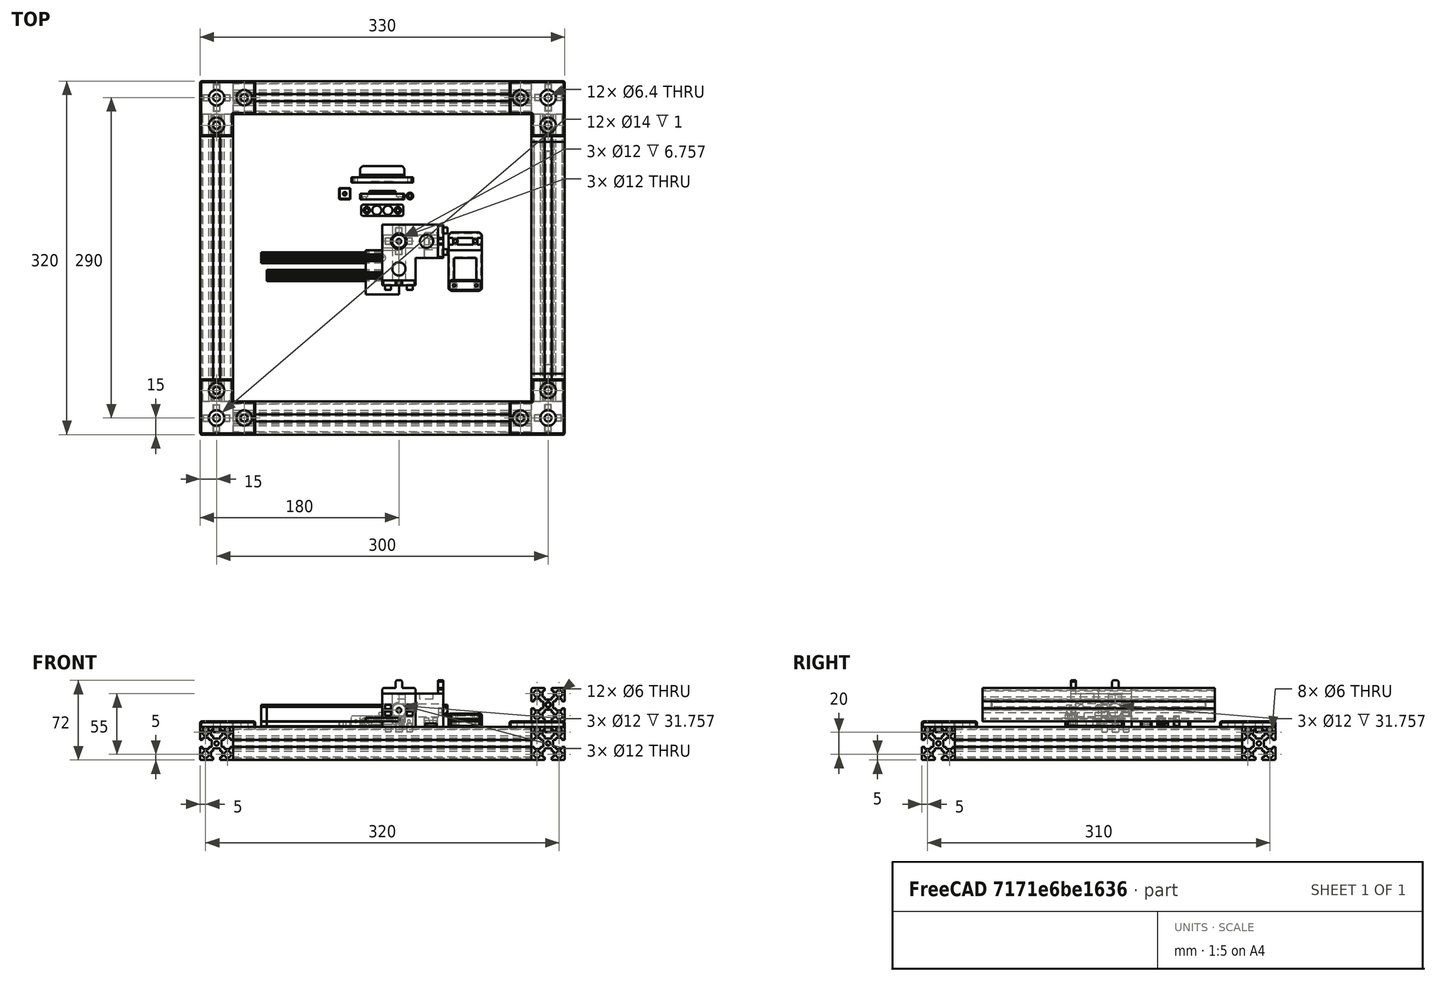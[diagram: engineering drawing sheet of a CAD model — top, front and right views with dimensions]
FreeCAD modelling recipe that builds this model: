
FCSTD DOCUMENT  (FreeCAD 0.18R16146 (Git))
Label: hophat-3030
License: All rights reserved
LicenseURL: http://en.wikipedia.org/wiki/All_rights_reserved
objects: Part::Box×32, Part::Feature×28, Part::MultiFuse×27, Part::Chamfer×27, Part::Cylinder×21, Part::Cut×17, Part::Fillet×2, Part::MultiCommon×1
note: 155 computed .brp shape members not serialized (recipe doc carries the construction recipe); baked Part::Feature solids carry a one-line shape summary decoded from their .brp

FEATURE [Part::Feature] Fusion025  label="extrusion-260-003"
  Placement = pos=(-150,-130,350) rot=(-1,0,0;1.5708rad)
  shape: bbox 30 x 260 x 30 mm, 63 faces (baked)
FEATURE [Part::Feature] Fusion032  label="extrusion-270-005"
  Placement = pos=(-135,-145,350) rot=(0,1,0;1.5708rad)
  shape: bbox 270 x 30 x 30 mm, 63 faces (baked)
FEATURE [Part::Feature] Fusion026  label="extrusion-260-004"
  Placement = pos=(150,-130,350) rot=(-1,0,0;1.5708rad)
  shape: bbox 30 x 260 x 30 mm, 63 faces (baked)
FEATURE [Part::Feature] Fusion031  label="extrusion-270-004"
  Placement = pos=(-135,145,350) rot=(0,1,0;1.5708rad)
  shape: bbox 270 x 30 x 30 mm, 63 faces (baked)
FEATURE [Part::MultiFuse] Fusion004003058  label="__top-framr-pref"
  Placement = pos=(0,0,-365) rot=(0,0,1;0rad)
  Shapes = -> [Fusion025,Fusion031,Fusion026,Fusion032]
FEATURE [Part::Feature] Fusion020006007003002004  label="top-joiner-002"
  Placement = pos=(-150,-145,370) rot=(0.707107,0.707107,0;3.14159rad)
  shape: bbox 50 x 50 x 10 mm, 87 faces (baked)
FEATURE [Part::Feature] Fusion020006007003002005  label="top-joiner-003"
  Placement = pos=(-150,145,370) rot=(1,0,0;3.14159rad)
  shape: bbox 50 x 50 x 10 mm, 87 faces (baked)
FEATURE [Part::Feature] Fusion020006007003002006  label="top-joiner-004"
  Placement = pos=(150,145,370) rot=(0.707107,-0.707107,0;3.14159rad)
  shape: bbox 50 x 50 x 10 mm, 87 faces (baked)
FEATURE [Part::Feature] Fusion020006007003002007  label="top-joiner-001"
  Placement = pos=(150,-145,370) rot=(0,1,0;3.14159rad)
  shape: bbox 50 x 50 x 10 mm, 87 faces (baked)
FEATURE [Part::Cylinder] Cylinder
  Angle = 360
  AttacherType = Attacher::AttachEngine3D
  Height = 10
  Radius = 1.25
FEATURE [Part::Cylinder] Cylinder001
  Angle = 360
  AttacherType = Attacher::AttachEngine3D
  Height = 3
  Placement = pos=(0,0,10) rot=(0,0,1;0rad)
  Radius = 3
FEATURE [Part::MultiFuse] Fusion020006007003002009  label="_M3-self-tapping"
  Shapes = -> [Cylinder001,Cylinder]
FEATURE [Part::Cylinder] Cylinder002
  Angle = 360
  AttacherType = Attacher::AttachEngine3D
  Height = 10
  Radius = 1.65
FEATURE [Part::Cylinder] Cylinder003
  Angle = 360
  AttacherType = Attacher::AttachEngine3D
  Height = 3
  Placement = pos=(0,0,10) rot=(0,0,1;0rad)
  Radius = 3
FEATURE [Part::MultiFuse] Fusion020006007003002010  label="_M3-outer-slot"
  Shapes = -> [Cylinder002,Cylinder003]
FEATURE [Part::Box] Box  label="Cube"
  AttacherType = Attacher::AttachEngine3D
  Height = 30
  Length = 30
  Width = 30
FEATURE [Part::Feature] Fusion020006007003002011  label="top-joiner-005"
  Placement = pos=(15,15,-5) rot=(0,0,1;0rad)
  shape: bbox 50 x 50 x 10 mm, 87 faces (baked)
FEATURE [Part::Box] Box001  label="Cube001"
  AttacherType = Attacher::AttachEngine3D
  Height = 30
  Length = 30
  Placement = pos=(0,-25,0) rot=(0,0,1;0rad)
  Width = 25
FEATURE [Part::Box] Box002  label="Cube002"
  AttacherType = Attacher::AttachEngine3D
  Height = 30
  Length = 25
  Placement = pos=(30,0,0) rot=(0,0,1;0rad)
  Width = 30
FEATURE [Part::Cylinder] Cylinder004
  Angle = 360
  AttacherType = Attacher::AttachEngine3D
  Height = 26
  Placement = pos=(15,15,4) rot=(0,0,1;0rad)
  Radius = 6
FEATURE [Part::Cylinder] Cylinder005
  Angle = 360
  AttacherType = Attacher::AttachEngine3D
  Height = 10
  Placement = pos=(45,15,15) rot=(0,1,0;1.5708rad)
  Radius = 2.2
FEATURE [Part::Cylinder] Cylinder006
  Angle = 360
  AttacherType = Attacher::AttachEngine3D
  Height = 10
  Placement = pos=(15,-15,15) rot=(1,0,0;1.5708rad)
  Radius = 2.2
FEATURE [Part::Cylinder] Cylinder007
  Angle = 360
  AttacherType = Attacher::AttachEngine3D
  Height = 51
  Placement = pos=(0,15,15) rot=(0,1,0;1.5708rad)
  Radius = 6
FEATURE [Part::Cylinder] Cylinder009
  Angle = 360
  AttacherType = Attacher::AttachEngine3D
  Height = 30
  Placement = pos=(15,15,0) rot=(0,0,1;0rad)
  Radius = 2.2
FEATURE [Part::Cylinder] Cylinder008
  Angle = 360
  AttacherType = Attacher::AttachEngine3D
  Height = 51
  Placement = pos=(15,30,15) rot=(1,0,0;1.5708rad)
  Radius = 6
FEATURE [Part::Cylinder] Cylinder010
  Angle = 360
  AttacherType = Attacher::AttachEngine3D
  Height = 5
  Placement = pos=(40,15,25) rot=(0,0,1;0rad)
  Radius = 6
FEATURE [Part::Cylinder] Cylinder011
  Angle = 360
  AttacherType = Attacher::AttachEngine3D
  Height = 5
  Placement = pos=(15,-10,25) rot=(0,0,1;0rad)
  Radius = 6
FEATURE [Part::MultiFuse] Fusion020006007003002012  label="bottom-cut-slot"
  Shapes = -> [Cylinder011,Cylinder010]
FEATURE [Part::Box] Box003  label="Cube003"
  AttacherType = Attacher::AttachEngine3D
  Height = 10
  Length = 5.3
  Placement = pos=(2.6,-24,10) rot=(0,0,1;0rad)
  Width = 5
FEATURE [Part::Box] Box004  label="Cube004"
  AttacherType = Attacher::AttachEngine3D
  Height = 10
  Length = 5.3
  Placement = pos=(22.1,-24,10) rot=(0,0,1;0rad)
  Width = 5
FEATURE [Part::MultiFuse] Fusion
  Shapes = -> [Box001,Box002,Box]
FEATURE [Part::MultiFuse] Fusion020006007003002013004  label="corner-inner-cut"
  Shapes = -> [Cylinder009,Cylinder006,Cylinder007,Cylinder005,Cylinder004,Cylinder008]
FEATURE [Part::Cut] Cut  label="corner-base"
  Base = -> Fusion
  Tool = -> Fusion020006007003002013004
FEATURE [Part::Box] Box005  label="Cube005"
  AttacherType = Attacher::AttachEngine3D
  Height = 6
  Length = 30
  Placement = pos=(0,-25,29) rot=(0,0,1;0rad)
  Width = 4.5
FEATURE [Part::Box] Box006  label="Cube006"
  AttacherType = Attacher::AttachEngine3D
  Height = 7
  Length = 6
  Placement = pos=(12,-25,35) rot=(0,0,1;0rad)
  Width = 4.5
FEATURE [Part::Box] Box007  label="Cube007"
  AttacherType = Attacher::AttachEngine3D
  Height = 10
  Length = 30
  Width = 30
FEATURE [Part::MultiCommon] Common
  Placement = pos=(30,0,7e-15) rot=(0,1,0;3.14159rad)
  Shapes = -> [Box007,Fusion020006007003002011]
FEATURE [Part::Chamfer] Chamfer005002
  Base = -> Box005
  Edges = 2 edges r=1: [Edge2,Edge6]
FEATURE [Part::MultiFuse] Fusion020006007003002013006002005002
  Shapes = -> [Box006,Chamfer005002]
FEATURE [Part::Feature] Fusion020006007003002013006002005002001  label="Fusion020006007003002013006002005003"
  Placement = pos=(30,-7e-15,0) rot=(0,0,1;1.5708rad)
  shape: bbox 4.5 x 30 x 13 mm, 14 faces (baked)
FEATURE [Part::Chamfer] Chamfer005003
  Base = -> Fusion020006007003002013006002005002001
  Edges = 2 edges r=1: [Edge31,Edge32]
FEATURE [Part::Chamfer] Chamfer005004
  Base = -> Fusion020006007003002013006002005002
  Edges = 2 edges r=1: [Edge31,Edge32]
FEATURE [Part::Feature] Fusion020006007003002013006002005002002010  label="210mm-extrusion-004"
  Placement = pos=(150,105,20) rot=(1,0,0;1.5708rad)
  shape: bbox 30 x 210 x 30 mm, 69 faces (baked)
FEATURE [Part::MultiFuse] Fusion020006007003002013006002005002002014
  Shapes = -> [Chamfer005004,Chamfer005003]
FEATURE [Part::MultiFuse] Fusion020006007003002013006002005002002015
  Placement = pos=(0,-5,0) rot=(0,0,1;0rad)
  Shapes = -> [Box004,Box003]
FEATURE [Part::Feature] Fusion020006007003002013006002005002002015001  label="Fusion020006007003002013006002005002002016"
  Placement = pos=(35,-7.8e-15,0) rot=(0,0,1;1.5708rad)
  shape: bbox 5 x 24.8 x 10 mm, 12 faces, 2 solids (baked)
FEATURE [Part::MultiFuse] Fusion020006007003002013006002005002002015002  label="side-aligner"
  Shapes = -> [Fusion020006007003002013006002005002002015001,Fusion020006007003002013006002005002002015]
FEATURE [Part::MultiFuse] Fusion020006007003002008  label="__top-joiner-pref"
  Placement = pos=(0,0,-365) rot=(0,0,1;0rad)
  Shapes = -> [Fusion020006007003002007,Fusion020006007003002004,Fusion020006007003002006,Fusion020006007003002005]
FEATURE [Part::Feature] Fusion020006007003002013006002005002002015002001  label="side-aligner001"
  shape: bbox 56.4 x 56.4 x 10 mm, 24 faces, 4 solids (baked)
FEATURE [Part::Feature] Cut001  label="corner-base001"
  shape: bbox 55 x 55 x 30 mm, 20 faces (baked)
FEATURE [Part::Chamfer] Chamfer
  Base = -> Fusion020006007003002013006002005002002015002001
  Edges = 4 edges r=4: [Edge10,Edge22,Edge34,Edge46]
FEATURE [Part::Fillet] Fillet
  Base = -> Cut001
  Edges = 10 edges r=1: [Edge31,Edge32,Edge33,Edge36,Edge38,Edge54,Edge55,Edge56,Edge57,Edge58]
FEATURE [Part::Chamfer] Chamfer005005
  Base = -> Fillet
  Edges = 3 edges r=1: [Edge23,Edge34,Edge76]
FEATURE [Part::MultiFuse] Fusion020006007003002013006002005002002015002002  label="top-r1"
  Shapes = -> [Chamfer005005,Chamfer,Common]
FEATURE [Part::Feature] Cut002  label="corner-base002"
  shape: bbox 55 x 55 x 30 mm, 20 faces (baked)
FEATURE [Part::Feature] Fusion020006007003002013006002005002002015002003  label="side-aligner002"
  shape: bbox 56.4 x 56.4 x 10 mm, 24 faces, 4 solids (baked)
FEATURE [Part::Chamfer] Chamfer005006
  Base = -> Fusion020006007003002013006002005002002015002003
  Edges = 4 edges r=4: [Edge9,Edge21,Edge33,Edge45]
FEATURE [Part::Fillet] Fillet001
  Base = -> Cut002
  Edges = 10 edges r=1: [Edge31,Edge32,Edge33,Edge36,Edge38,Edge54,Edge55,Edge56,Edge57,Edge58]
FEATURE [Part::MultiFuse] Fusion020006007003002013006002005002002015002004
  Shapes = -> [Fillet001,Chamfer005006,Fusion020006007003002013006002005002002014]
FEATURE [Part::Chamfer] Chamfer005007
  Base = -> Fusion020006007003002013006002005002002015002004
  Edges = 3 edges r=1: [Edge35,Edge113,Edge145]
FEATURE [Part::Cut] Cut003  label="bottom-r1"
  Base = -> Chamfer005007
  Tool = -> Fusion020006007003002012
FEATURE [Part::Box] Box008  label="Cube008"
  AttacherType = Attacher::AttachEngine3D
  Height = 5.2
  Length = 38
  Placement = pos=(-19,-5,0) rot=(0,0,1;0rad)
  Width = 10
FEATURE [Part::Cylinder] Cylinder012
  Angle = 360
  AttacherType = Attacher::AttachEngine3D
  Height = 3
  Placement = pos=(-5,0,2.2) rot=(0,0,1;0rad)
  Radius = 4.15
FEATURE [Part::Cylinder] Cylinder013
  Angle = 360
  AttacherType = Attacher::AttachEngine3D
  Height = 3
  Placement = pos=(5,0,2.2) rot=(0,0,1;0rad)
  Radius = 4.15
FEATURE [Part::Cylinder] Cylinder014
  Angle = 360
  AttacherType = Attacher::AttachEngine3D
  Height = 10
  Placement = pos=(-14,0,0) rot=(0,0,1;0rad)
  Radius = 1.7
FEATURE [Part::Cylinder] Cylinder015
  Angle = 360
  AttacherType = Attacher::AttachEngine3D
  Height = 10
  Placement = pos=(14,0,0) rot=(0,0,1;0rad)
  Radius = 1.7
FEATURE [Part::Cylinder] Cylinder016
  Angle = 360
  AttacherType = Attacher::AttachEngine3D
  Height = 2
  Placement = pos=(14,0,0) rot=(0,0,1;0rad)
  Radius = 3
FEATURE [Part::Cylinder] Cylinder017
  Angle = 360
  AttacherType = Attacher::AttachEngine3D
  Height = 2
  Placement = pos=(-14,0,0) rot=(0,0,1;0rad)
  Radius = 3
FEATURE [Part::MultiFuse] Fusion020006007003002013006002005002002015002005
  Placement = pos=(0,0,4) rot=(0,0,1;0rad)
  Shapes = -> [Cylinder017,Cylinder016]
FEATURE [Part::MultiFuse] Fusion020006007003002013006002005002002015002006
  Shapes = -> [Cylinder014,Cylinder015]
FEATURE [Part::Chamfer] Chamfer005008
  Base = -> Box008
  Edges = 4 edges r=1: [Edge1,Edge3,Edge5,Edge7]
FEATURE [Part::Cut] Cut004
  Base = -> Chamfer005008
  Tool = -> Fusion020006007003002013006002005002002015002006
FEATURE [Part::Cut] Cut005
  Base = -> Cut004
  Tool = -> Fusion020006007003002013006002005002002015002005
FEATURE [Part::MultiFuse] Fusion020006007003002013006002005002002015002007
  Shapes = -> [Cylinder013,Cylinder012]
FEATURE [Part::Cut] Cut006  label="round-magnet-mounter"
  Base = -> Cut005
  Placement = pos=(0,43,0) rot=(0,0,1;0rad)
  Tool = -> Fusion020006007003002013006002005002002015002007
FEATURE [Part::Box] Box009  label="Cube009"
  AttacherType = Attacher::AttachEngine3D
  Height = 5.2
  Length = 10
  Placement = pos=(-5,-5,0) rot=(0,0,1;0rad)
  Width = 10
FEATURE [Part::Cylinder] Cylinder018
  Angle = 360
  AttacherType = Attacher::AttachEngine3D
  Height = 10
  Radius = 1.25
FEATURE [Part::Chamfer] Chamfer005009
  Base = -> Box009
  Edges = 11 edges r=0.4: [Edge1,Edge2,Edge3,Edge4,Edge5,Edge6,Edge8,Edge9,Edge10,Edge11,Edge12]
FEATURE [Part::Cut] Cut007
  Base = -> Chamfer005009
  Tool = -> Cylinder018
FEATURE [Part::Chamfer] Chamfer005010  label="self-tapping-nut"
  Base = -> Cut007
  Edges = 2 edges r=0.4: [Edge25,Edge30]
  Placement = pos=(-34,58,0) rot=(0,0,1;0rad)
FEATURE [Part::Box] Box010  label="Cube010"
  AttacherType = Attacher::AttachEngine3D
  Height = 6
  Length = 24
  Placement = pos=(-12,0,2) rot=(0,0,1;0rad)
  Width = 2.6
FEATURE [Part::Box] Box011  label="Cube011"
  AttacherType = Attacher::AttachEngine3D
  Height = 10
  Length = 40
  Placement = pos=(-20,-5,0) rot=(0,0,1;0rad)
  Width = 5
FEATURE [Part::Box] Box012  label="Cube012"
  AttacherType = Attacher::AttachEngine3D
  Height = 6
  Length = 20
  Placement = pos=(-10,0,2) rot=(0,0,1;0rad)
  Width = 1.5
FEATURE [Part::Cut] Cut008
  Base = -> Box010
  Tool = -> Box012
FEATURE [Part::Feature] Fusion020006007003002010001  label="_M3-outer-slot001"
  Placement = pos=(16,-13,5) rot=(-1,0,0;1.5708rad)
  shape: bbox 6 x 13 x 6 mm, 5 faces (baked)
FEATURE [Part::Feature] Fusion020006007003002013006002005002002015002008  label="_M3-outer-slot002"
  Placement = pos=(-16,-13,5) rot=(-1,0,0;1.5708rad)
  shape: bbox 6 x 13 x 6 mm, 5 faces (baked)
FEATURE [Part::Chamfer] Chamfer005011
  Base = -> Box011
  Edges = 4 edges r=1: [Edge2,Edge4,Edge6,Edge8]
FEATURE [Part::MultiFuse] Fusion020006007003002013006002005002002015002009
  Shapes = -> [Fusion020006007003002013006002005002002015002008,Fusion020006007003002010001]
FEATURE [Part::Cut] Cut009
  Base = -> Chamfer005011
  Tool = -> Fusion020006007003002013006002005002002015002009
FEATURE [Part::MultiFuse] Fusion020006007003002013006002005002002015002010  label="rec-magnet-mounter"
  Placement = pos=(0,58,0) rot=(0,0,1;0rad)
  Shapes = -> [Cut009,Cut008]
FEATURE [Part::Box] Box013  label="Cube013"
  AttacherType = Attacher::AttachEngine3D
  Height = 6
  Length = 20
  Placement = pos=(-10,0,2) rot=(0,0,1;0rad)
  Width = 1.5
FEATURE [Part::Box] Box014  label="Cube014"
  AttacherType = Attacher::AttachEngine3D
  Height = 10
  Length = 56
  Placement = pos=(-28,0,0) rot=(0,0,1;0rad)
  Width = 5
FEATURE [Part::Box] Box015  label="Cube015"
  AttacherType = Attacher::AttachEngine3D
  Height = 5
  Length = 40
  Placement = pos=(-20,5,0) rot=(0,0,1;0rad)
  Width = 10
FEATURE [Part::Feature] Fusion020006007003002009001  label="_M3-self-tapping001"
  Placement = pos=(-24,10,5) rot=(1,0,0;1.5708rad)
  shape: bbox 6 x 13 x 6 mm, 5 faces (baked)
FEATURE [Part::Feature] Fusion020006007003002013006002005002002015002011  label="_M3-self-tapping002"
  Placement = pos=(24,10,5) rot=(1,0,0;1.5708rad)
  shape: bbox 6 x 13 x 6 mm, 5 faces (baked)
FEATURE [Part::Chamfer] Chamfer005012
  Base = -> Box014
  Edges = 4 edges r=1: [Edge2,Edge4,Edge6,Edge8]
FEATURE [Part::MultiFuse] Fusion020006007003002013006002005002002015002012
  Shapes = -> [Fusion020006007003002009001,Fusion020006007003002013006002005002002015002011]
FEATURE [Part::Cut] Cut010
  Base = -> Chamfer005012
  Tool = -> Fusion020006007003002013006002005002002015002012
FEATURE [Part::Chamfer] Chamfer005013
  Base = -> Box015
  Edges = 2 edges r=2: [Edge3,Edge7]
FEATURE [Part::MultiFuse] Fusion020006007003002013006002005002002015002013
  Shapes = -> [Cut010,Chamfer005013]
FEATURE [Part::Chamfer] Chamfer005014
  Base = -> Fusion020006007003002013006002005002002015002013
  Edges = 1 edges r=2: [Edge20]
FEATURE [Part::Cut] Cut011  label="rec-magnet-handle"
  Base = -> Chamfer005014
  Placement = pos=(0,68,0) rot=(0,0,1;0rad)
  Tool = -> Box013
FEATURE [Part::Cylinder] Cylinder019
  Angle = 360
  AttacherType = Attacher::AttachEngine3D
  Height = 3
  Radius = 3
FEATURE [Part::Cylinder] Cylinder020
  Angle = 360
  AttacherType = Attacher::AttachEngine3D
  Height = 3
  Radius = 1.65
FEATURE [Part::Cut] Cut012
  Base = -> Cylinder019
  Tool = -> Cylinder020
FEATURE [Part::Chamfer] Chamfer005015  label="3mm-spacer"
  Base = -> Cut012
  Edges = 2 edges r=0.4: [Edge1,Edge3]
  Placement = pos=(25,56,0) rot=(0,0,1;0rad)
FEATURE [Part::Box] Box016  label="Cube016"
  AttacherType = Attacher::AttachEngine3D
  Height = 5
  Length = 30
  Placement = pos=(-15,-30,0) rot=(0,0,1;0rad)
  Width = 53
FEATURE [Part::Box] Box017  label="Cube017"
  AttacherType = Attacher::AttachEngine3D
  Height = 3
  Length = 30
  Placement = pos=(-15,-33,5) rot=(0,0,1;0rad)
  Width = 40
FEATURE [Part::Box] Box018  label="Cube018"
  AttacherType = Attacher::AttachEngine3D
  Height = 3
  Length = 30
  Placement = pos=(-15,7,5) rot=(0,0,1;0rad)
  Width = 16
FEATURE [Part::Box] Box019  label="Cube019"
  AttacherType = Attacher::AttachEngine3D
  Height = 5
  Length = 20
  Placement = pos=(-10,-20,0) rot=(0,0,1;0rad)
  Width = 20
FEATURE [Part::Box] Box020  label="Cube020"
  AttacherType = Attacher::AttachEngine3D
  Height = 2
  Length = 4
  Placement = pos=(-15,12,8) rot=(0,0,1;0rad)
  Width = 6
FEATURE [Part::Feature] Fusion020006007003002010002  label="_M3-outer-slot003"
  Placement = pos=(-9,15,13) rot=(0,1,0;3.14159rad)
  shape: bbox 6 x 6 x 13 mm, 5 faces (baked)
FEATURE [Part::Feature] Fusion020006007003002013006002005002002015002014  label="_M3-outer-slot004"
  Placement = pos=(9,15,13) rot=(0,1,0;3.14159rad)
  shape: bbox 6 x 6 x 13 mm, 5 faces (baked)
FEATURE [Part::Box] Box021  label="Cube021"
  AttacherType = Attacher::AttachEngine3D
  Height = 2
  Length = 14
  Placement = pos=(-7,12,8) rot=(0,0,1;0rad)
  Width = 6
FEATURE [Part::Box] Box022  label="Cube022"
  AttacherType = Attacher::AttachEngine3D
  Height = 2
  Length = 4
  Placement = pos=(11,12,8) rot=(0,0,1;0rad)
  Width = 6
FEATURE [Part::MultiFuse] Fusion020006007003002013006002005002002015002016
  Shapes = -> [Fusion020006007003002010002,Fusion020006007003002013006002005002002015002014]
FEATURE [Part::Feature] Fusion020006007003002013006002005002002015002016001  label="Fusion020006007003002013006002005002002015002017"
  Placement = pos=(0,0,2) rot=(0,0,1;0rad)
  shape: bbox 24 x 6 x 13 mm, 10 faces, 2 solids (baked)
FEATURE [Part::MultiFuse] Fusion020006007003002013006002005002002015002016002
  Shapes = -> [Fusion020006007003002013006002005002002015002016001,Fusion020006007003002013006002005002002015002016]
FEATURE [Part::Cut] Cut013
  Base = -> Box016
  Tool = -> Box019
FEATURE [Part::MultiFuse] Fusion020006007003002013006002005002002015002016003
  Shapes = -> [Cut013,Box018,Box020,Box021,Box022]
FEATURE [Part::Cut] Cut014
  Base = -> Fusion020006007003002013006002005002002015002016003
  Tool = -> Fusion020006007003002013006002005002002015002016002
FEATURE [Part::Feature] Fusion020006007003002010003  label="_M3-outer-slot005"
  Placement = pos=(10,-25,12) rot=(0,1,0;3.14159rad)
  shape: bbox 6 x 6 x 13 mm, 5 faces (baked)
FEATURE [Part::Feature] Fusion020006007003002013006002005002002015002016004  label="_M3-outer-slot006"
  Placement = pos=(-10,-25,12) rot=(0,1,0;3.14159rad)
  shape: bbox 6 x 6 x 13 mm, 5 faces (baked)
FEATURE [Part::Chamfer] Chamfer005016
  Base = -> Cut014
  Edges = 4 edges r=2: [Edge30,Edge32,Edge67,Edge69]
FEATURE [Part::Chamfer] Chamfer005017
  Base = -> Chamfer005016
  Edges = 4 edges r=1: [Edge96,Edge97,Edge98,Edge99]
FEATURE [Part::Chamfer] Chamfer005018
  Base = -> Chamfer005017
  Edges = 8 edges r=1: [Edge33,Edge35,Edge40,Edge44,Edge46,Edge47,Edge48,Edge49]
FEATURE [Part::MultiFuse] Fusion020006007003002013006002005002002015002016005
  Shapes = -> [Fusion020006007003002013006002005002002015002016004,Fusion020006007003002010003]
FEATURE [Part::Chamfer] Chamfer005019
  Base = -> Chamfer005018
  Edges = 8 edges r=1: [Edge42,Edge43,Edge44,Edge45,Edge46,Edge47,Edge48,Edge49]
FEATURE [Part::Cut] Cut015  label="bowden-slot-outer"
  Base = -> Chamfer005019
  Placement = pos=(75,0,0) rot=(0,0,1;0rad)
  Tool = -> Fusion020006007003002013006002005002002015002016005
FEATURE [Part::Box] Box023  label="Cube023"
  AttacherType = Attacher::AttachEngine3D
  Height = 5
  Length = 30
  Placement = pos=(-15,-30,7) rot=(0,0,1;0rad)
  Width = 10
FEATURE [Part::Chamfer] Chamfer005020
  Base = -> Box023
  Edges = 4 edges r=2: [Edge1,Edge3,Edge5,Edge7]
FEATURE [Part::Feature] Fusion020006007003002009002  label="_M3-self-tapping003"
  Placement = pos=(10,-25,3) rot=(0,0,1;0rad)
  shape: bbox 6 x 6 x 13 mm, 5 faces (baked)
FEATURE [Part::Feature] Fusion020006007003002013006002005002002015002016006  label="_M3-self-tapping004"
  Placement = pos=(-10,-25,3) rot=(0,0,1;0rad)
  shape: bbox 6 x 6 x 13 mm, 5 faces (baked)
FEATURE [Part::Cut] Cut016
  Base = -> Chamfer005020
  Tool = -> Fusion020006007003002013006002005002002015002016006
FEATURE [Part::Cut] Cut017
  Base = -> Cut016
  Tool = -> Fusion020006007003002009002
FEATURE [Part::Chamfer] Chamfer005021  label="bowden-slot-inner"
  Base = -> Cut017
  Edges = 8 edges r=1: [Edge1,Edge5,Edge6,Edge7,Edge8,Edge9,Edge10,Edge11]
  Placement = pos=(75,0,0) rot=(0,0,1;0rad)
FEATURE [Part::Box] Box024  label="Cube024"
  AttacherType = Attacher::AttachEngine3D
  Height = 3
  Length = 12
  Width = 23
FEATURE [Part::Box] Box025  label="Cube025"
  AttacherType = Attacher::AttachEngine3D
  Height = 3
  Length = 12
  Placement = pos=(0,7.5,3) rot=(0,0,1;0rad)
  Width = 15.5
FEATURE [Part::Box] Box026  label="Cube026"
  AttacherType = Attacher::AttachEngine3D
  Height = 2
  Length = 4
  Placement = pos=(0,12,6) rot=(0,0,1;0rad)
  Width = 6
FEATURE [Part::Box] Box027  label="Cube027"
  AttacherType = Attacher::AttachEngine3D
  Height = 2
  Length = 4
  Placement = pos=(8,12,6) rot=(0,0,1;0rad)
  Width = 6
FEATURE [Part::Feature] Fusion020006007003002010004  label="_M3-outer-slot007"
  Placement = pos=(6,15,13) rot=(0,1,0;3.14159rad)
  shape: bbox 6 x 6 x 13 mm, 5 faces (baked)
FEATURE [Part::MultiFuse] Fusion020006007003002013006002005002002015002016007
  Shapes = -> [Box024,Box025,Box026,Box027]
FEATURE [Part::Chamfer] Chamfer005022
  Base = -> Fusion020006007003002013006002005002002015002016007
  Edges = 4 edges r=1: [Edge1,Edge4,Edge7,Edge17]
FEATURE [Part::Chamfer] Chamfer005023
  Base = -> Chamfer005022
  Edges = 8 edges r=0.4: [Edge4,Edge11,Edge18,Edge19,Edge20,Edge21,Edge22,Edge23]
FEATURE [Part::Cut] Cut018  label="panel-clip"
  Base = -> Chamfer005023
  Placement = pos=(38,0,0) rot=(0,0,1;0rad)
  Tool = -> Fusion020006007003002010004
FEATURE [Part::Box] Box028  label="Cube028"
  AttacherType = Attacher::AttachEngine3D
  Height = 104.5
  Length = 10
  Placement = pos=(-5,0,0) rot=(0,0,1;0rad)
  Width = 5
FEATURE [Part::Box] Box029  label="Cube029"
  AttacherType = Attacher::AttachEngine3D
  Height = 104.5
  Length = 6
  Placement = pos=(-3,5,0) rot=(0,0,1;0rad)
  Width = 15
FEATURE [Part::Box] Box030  label="Cube030"
  AttacherType = Attacher::AttachEngine3D
  Height = 109.5
  Length = 6
  Placement = pos=(-3,5,0) rot=(0,0,1;0rad)
  Width = 15
FEATURE [Part::Box] Box031  label="Cube031"
  AttacherType = Attacher::AttachEngine3D
  Height = 109.5
  Length = 10
  Placement = pos=(-5,0,0) rot=(0,0,1;0rad)
  Width = 5
FEATURE [Part::MultiFuse] Fusion020006007003002013006002005002002015002016008
  Shapes = -> [Box031,Box030]
FEATURE [Part::Chamfer] Chamfer005024
  Base = -> Fusion020006007003002013006002005002002015002016008
  Edges = 2 edges r=2: [Edge22,Edge26]
FEATURE [Part::Chamfer] Chamfer005025  label="109d5-channel"
  Base = -> Chamfer005024
  Edges = 4 edges r=0.4: [Edge24,Edge26,Edge29,Edge30]
  Placement = pos=(0,0,0) rot=(-0.57735,0.57735,0.57735;4.18879rad)
FEATURE [Part::MultiFuse] Fusion020006007003002013006002005002002015002016009
  Shapes = -> [Box028,Box029]
FEATURE [Part::Chamfer] Chamfer005026
  Base = -> Fusion020006007003002013006002005002002015002016009
  Edges = 2 edges r=2: [Edge22,Edge26]
FEATURE [Part::Chamfer] Chamfer005027  label="104d5-channel"
  Base = -> Chamfer005026
  Edges = 4 edges r=0.4: [Edge24,Edge26,Edge29,Edge30]
  Placement = pos=(-3.6e-15,-16,3.6e-15) rot=(-0.57735,0.57735,0.57735;4.18879rad)
